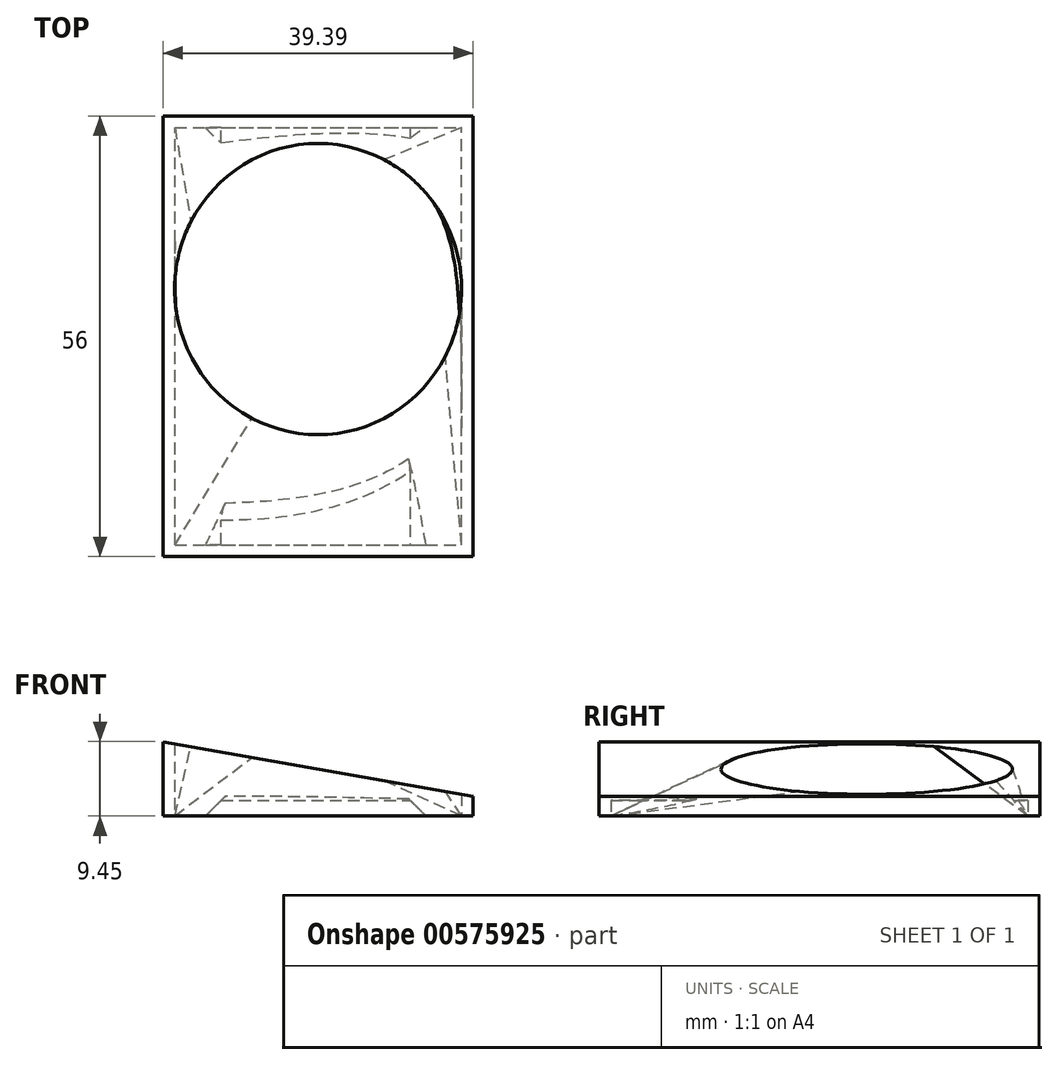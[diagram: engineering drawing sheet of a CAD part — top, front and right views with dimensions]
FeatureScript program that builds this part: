
annotation { "Feature Type Name" : "Feature", "Feature Type Description" : "" }
export const myFeature = defineFeature(function(context is Context, id is Id, definition is map)
    precondition{}
    {
        {
            var Q0;
            Q0=qCreatedBy(makeId("Front.planeOp"),FACE);
            var sketch = newSketch(context, id + "F0", { "sketchPlane" : qUnion([Q0])});
            skLineSegment(sketch, "E0", {"start": v(0, 0) * mm, "end": v(0, 2.5) * mm});
            skLineSegment(sketch, "E1", {"start": v(0, 2.5) * mm, "end": v(-39.4, 9.45) * mm});
            skLineSegment(sketch, "E2", {"start": v(-39.4, 9.45) * mm, "end": v(-39.4, 0) * mm});
            skLineSegment(sketch, "E3", {"start": v(-39.4, 0) * mm, "end": v(0, 0) * mm});
            skSolve(sketch);
        }
        {
            var Q0;
            Q0 = qSketchRegion(id + "F0", true);
            extrude(context, id + "F1", {"entities" : qUnion([Q0]), "depth" : 56 * mm, "offsetDistance" : 25 * mm});
        }
        {
            var Q0;
            Q0=makeQuery(id+"F1.opExtrude","SWEPT_FACE",FACE,{"disambiguationData":[OSD([sQuery(id+"F0.wireOp",EDGE,"E1")])]});
            var sketch = newSketch(context, id + "F2", { "sketchPlane" : qUnion([Q0])});
            skCircle(sketch, "E4", {"center": v(-20.43, -22) * mm, "radius": 18.5 * mm});
            skPoint(sketch, "E4.centerSnap0", {"position": v(-20.43, -56) * mm});
            skSolve(sketch);
        }
        {
            var Q0;
            Q0=qCreatedBy(makeId("Top.planeOp"),FACE);
            var sketch = newSketch(context, id + "F3", { "sketchPlane" : qUnion([Q0])});
            skLineSegment(sketch, "E5.bottom", {"start": v(-37.9, -54.5) * mm, "end": v(-1.5, -54.5) * mm});
            skLineSegment(sketch, "E5.top", {"start": v(-37.9, -1.5) * mm, "end": v(-1.5, -1.5) * mm});
            skLineSegment(sketch, "E5.left", {"start": v(-37.9, -54.5) * mm, "end": v(-37.9, -1.5) * mm});
            skLineSegment(sketch, "E5.right", {"start": v(-1.5, -54.5) * mm, "end": v(-1.5, -1.5) * mm});
            skSolve(sketch);
        }
        {
            var Q1;
            Q1 = qSketchRegion(id + "F3", true);
            var Q2;
            Q2 = qSketchRegion(id + "F2", true);
            loft(context, id + "F4", {"operationType" : NewBodyOperationType.REMOVE, "sheetProfilesArray" : [{ "sheetProfileEntities" : qUnion([Q1]) }, { "sheetProfileEntities" : qUnion([Q2]) }]});
        }
        {
            var Q0;
            Q0=qCreatedBy(makeId("Right.planeOp"),FACE);
            var sketch = newSketch(context, id + "F5", { "sketchPlane" : qUnion([Q0])});
            skLineSegment(sketch, "E6", {"start": v(-54.5, 0) * mm, "end": v(-54.5, 2) * mm});
            skLineSegment(sketch, "E7", {"start": v(-54.5, 2) * mm, "end": v(-37.34, 2) * mm});
            skLineSegment(sketch, "E8", {"start": v(-37.34, 2) * mm, "end": v(-37.34, -3.53) * mm});
            skLineSegment(sketch, "E9", {"start": v(-37.34, -3.53) * mm, "end": v(-54.5, -3.53) * mm});
            skLineSegment(sketch, "E10", {"start": v(-54.5, -3.53) * mm, "end": v(-54.5, 0) * mm});
            skLineSegment(sketch, "E11.bottom", {"start": v(-1.5, 2) * mm, "end": v(-12.34, 2) * mm});
            skLineSegment(sketch, "E11.top", {"start": v(-1.5, -3.53) * mm, "end": v(-12.34, -3.53) * mm});
            skLineSegment(sketch, "E11.left", {"start": v(-1.5, 2) * mm, "end": v(-1.5, -3.53) * mm});
            skLineSegment(sketch, "E11.right", {"start": v(-12.34, 2) * mm, "end": v(-12.34, -3.53) * mm});
            skSolve(sketch);
        }
        {
            var Q0;
            Q0 = qSketchRegion(id + "F5", true);
            extrude(context, id + "F6", {"entities" : qUnion([Q0]), "operationType" : NewBodyOperationType.REMOVE, "oppositeDirection" : true, "depth" : 34 * mm, "offsetDistance" : 25 * mm, "hasSecondDirection" : true, "secondDirectionOppositeDirection" : true, "secondDirectionDepth" : 6 * mm});
        }
        {
            var Q0;
            Q0=makeQuery(id+"F6.boolean.opBoolean","COPY",EDGE,{"derivedFrom":makeQuery(id+"F6.opExtrude","CAP_EDGE",EDGE,{"disambiguationData":[OSD([sQuery(id+"F5.wireOp",EDGE,"E7")])],"isStart":false})});
            var Q1;
            Q1=makeQuery(id+"F6.boolean.opBoolean","COPY",EDGE,{"derivedFrom":makeQuery(id+"F6.opExtrude","CAP_EDGE",EDGE,{"disambiguationData":[OSD([sQuery(id+"F5.wireOp",EDGE,"E7")])],"isStart":true})});
            var Q2;
            Q2=makeQuery(id+"F6.boolean.opBoolean","COPY",EDGE,{"derivedFrom":makeQuery(id+"F6.opExtrude","CAP_EDGE",EDGE,{"disambiguationData":[OSD([sQuery(id+"F5.wireOp",EDGE,"E11.bottom")])],"isStart":true})});
            var Q3;
            Q3=makeQuery(id+"F6.boolean.opBoolean","COPY",EDGE,{"derivedFrom":makeQuery(id+"F6.opExtrude","CAP_EDGE",EDGE,{"disambiguationData":[OSD([sQuery(id+"F5.wireOp",EDGE,"E11.bottom")])],"isStart":false})});
            chamfer(context, id + "F7", {"entities" : qUnion([Q0, Q1, Q2, Q3]), "width" : 2 * mm, "tangentPropagation" : true});
        }
        {
            var Q0;
            Q0=makeQuery(id+"F6.boolean.opBoolean","INTERSECT",EDGE,{"derivedFrom":[makeQuery(id+"F4.boolean.opBoolean","COPY",FACE,{"derivedFrom":makeQuery(id+"F4.opLoft","SWEPT_FACE",FACE,{"disambiguationData":[OSD([sQuery(id+"F2.wireOp",EDGE,"E4"),sQuery(id+"F3.wireOp",EDGE,"E5.bottom"),sQuery(id+"F3.wireOp",EDGE,"E5.left"),sQuery(id+"F3.wireOp",EDGE,"E5.right")])]})}),makeQuery(id+"F6.opExtrude","SWEPT_FACE",FACE,{"disambiguationData":[OSD([sQuery(id+"F5.wireOp",EDGE,"E7")])]})]});
            fillet(context, id + "F8", {"entities" : qUnion([Q0]), "radius" : 5 * mm, "tangentPropagation" : true, "allowEdgeOverflow" : false});
        }
    });
